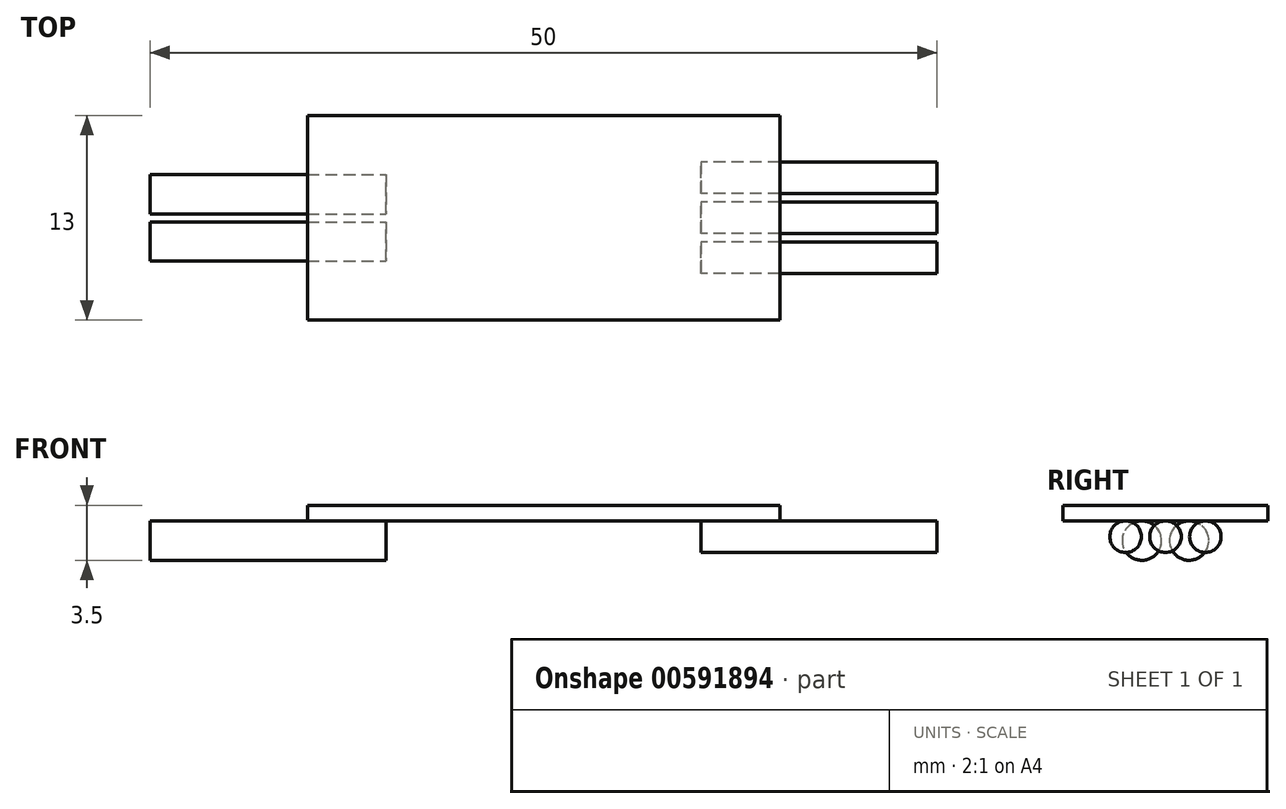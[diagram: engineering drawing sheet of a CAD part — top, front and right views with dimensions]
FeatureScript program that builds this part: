
annotation { "Feature Type Name" : "Feature", "Feature Type Description" : "" }
export const myFeature = defineFeature(function(context is Context, id is Id, definition is map)
    precondition{}
    {
        {
            var Q0;
            Q0=qCreatedBy(makeId("Top.planeOp"),FACE);
            var sketch = newSketch(context, id + "F0", { "sketchPlane" : qUnion([Q0])});
            skLineSegment(sketch, "E0.bottom", {"start": v(15, 6.5) * mm, "end": v(-15, 6.5) * mm});
            skLineSegment(sketch, "E0.top", {"start": v(15, -6.5) * mm, "end": v(-15, -6.5) * mm});
            skLineSegment(sketch, "E0.left", {"start": v(15, 6.5) * mm, "end": v(15, -6.5) * mm});
            skLineSegment(sketch, "E0.right", {"start": v(-15, 6.5) * mm, "end": v(-15, -6.5) * mm});
            skPoint(sketch, "E0.middle", {"position": v(0, 0) * mm});
            skSolve(sketch);
        }
        {
            var Q0;
            Q0 = qSketchRegion(id + "F0", true);
            extrude(context, id + "F1", {"entities" : qUnion([Q0]), "depth" : 1 * mm, "offsetDistance" : 25 * mm});
        }
        {
            var Q0;
            Q0=makeQuery(id+"F1.opExtrude","SWEPT_FACE",FACE,{"disambiguationData":[OSD([sQuery(id+"F0.wireOp",EDGE,"E0.left")])]});
            var sketch = newSketch(context, id + "F2", { "sketchPlane" : qUnion([Q0])});
            skCircle(sketch, "E1", {"center": v(-2.53, -1) * mm, "radius": 1 * mm});
            skCircle(sketch, "E2", {"center": v(0, -1) * mm, "radius": 1 * mm});
            skCircle(sketch, "E3", {"center": v(2.53, -1) * mm, "radius": 1 * mm});
            skLineSegment(sketch, "E4", {"start": v(-2.53, -1) * mm, "end": v(-3.3, -0.37) * mm, "construction": true});
            skLineSegment(sketch, "E5", {"start": v(0, -1) * mm, "end": v(-0.8, -0.4) * mm, "construction": true});
            skLineSegment(sketch, "E6", {"start": v(2.53, -1) * mm, "end": v(1.78, -0.35) * mm, "construction": true});
            skLineSegment(sketch, "E7", {"start": v(-2.53, -1) * mm, "end": v(0, -1) * mm, "construction": true});
            skLineSegment(sketch, "E8", {"start": v(2.53, -1) * mm, "end": v(0, -1) * mm, "construction": true});
            skLineSegment(sketch, "E9", {"start": v(0, 0) * mm, "end": v(0, -1) * mm, "construction": true});
            skSolve(sketch);
        }
        {
            var Q0;
            Q0 = qSketchRegion(id + "F2", true);
            extrude(context, id + "F3", {"entities" : qUnion([Q0]), "depth" : 10 * mm, "offsetDistance" : 25 * mm, "hasSecondDirection" : true, "secondDirectionOppositeDirection" : true, "secondDirectionDepth" : 5 * mm});
        }
        {
            var Q0;
            Q0=makeQuery(id+"F1.opExtrude","SWEPT_FACE",FACE,{"disambiguationData":[OSD([sQuery(id+"F0.wireOp",EDGE,"E0.right")])]});
            var sketch = newSketch(context, id + "F4", { "sketchPlane" : qUnion([Q0])});
            skCircle(sketch, "E10", {"center": v(-1.5, -1.25) * mm, "radius": 1.25 * mm});
            skCircle(sketch, "E11", {"center": v(1.5, -1.25) * mm, "radius": 1.25 * mm});
            skLineSegment(sketch, "E12", {"start": v(-1.5, -1.25) * mm, "end": v(1.5, -1.25) * mm, "construction": true});
            skLineSegment(sketch, "E13", {"start": v(-1.5, -1.25) * mm, "end": v(-1.5, 0) * mm, "construction": true});
            skLineSegment(sketch, "E14", {"start": v(1.5, -1.25) * mm, "end": v(1.5, 0) * mm, "construction": true});
            skPoint(sketch, "E15", {"position": v(0, -1.25) * mm});
            skLineSegment(sketch, "E16", {"start": v(0, -1.25) * mm, "end": v(0, 0) * mm, "construction": true});
            skSolve(sketch);
        }
        {
            var Q0;
            Q0 = qSketchRegion(id + "F4", true);
            extrude(context, id + "F5", {"entities" : qUnion([Q0]), "depth" : 10 * mm, "offsetDistance" : 25 * mm, "hasSecondDirection" : true, "secondDirectionOppositeDirection" : true, "secondDirectionDepth" : 5 * mm});
        }
    });
